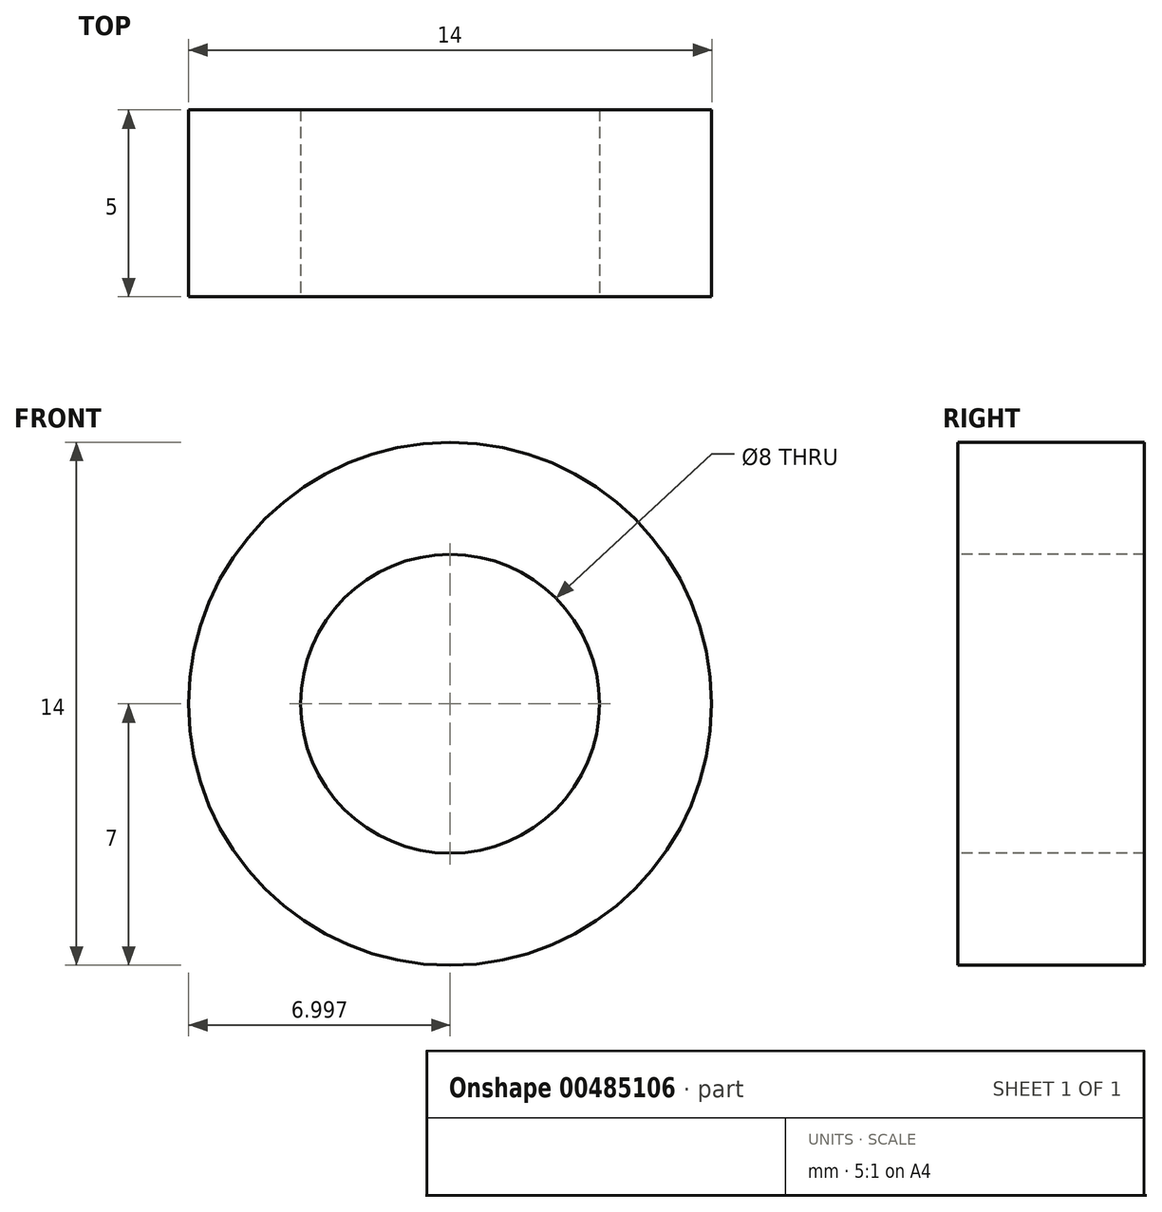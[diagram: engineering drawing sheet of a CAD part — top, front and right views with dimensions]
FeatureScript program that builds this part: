
annotation { "Feature Type Name" : "Feature", "Feature Type Description" : "" }
export const myFeature = defineFeature(function(context is Context, id is Id, definition is map)
    precondition{}
    {
        {
            var Q0;
            Q0=qCreatedBy(makeId("Front.planeOp"),FACE);
            var sketch = newSketch(context, id + "F0", { "sketchPlane" : qUnion([Q0])});
            skCircle(sketch, "E0", {"center": v(-0.28, 0.85) * mm, "radius": 4 * mm});
            skCircle(sketch, "E1", {"center": v(-0.28, 0.85) * mm, "radius": 7 * mm});
            skSolve(sketch);
        }
        {
            var Q0;
            Q0=makeQuery(id+"F0.imprint","IMPRINT",FACE,{"disambiguationData":[TD([[makeQuery(id+"F0.imprint","IMPRINT",EDGE,{"derivedFrom":sQuery(id+"F0.wireOp",EDGE,"E0")}),-1.0]])]});
            extrude(context, id + "F1", {"entities" : qUnion([Q0]), "oppositeDirection" : true, "depth" : 5 * mm});
        }
    });
